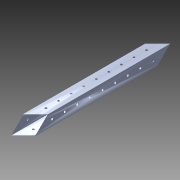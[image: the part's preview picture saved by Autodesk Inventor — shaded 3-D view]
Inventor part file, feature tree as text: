
AUTODESK INVENTOR PART (.ipt)
format: ipt  version: 2014 SP1 (Build 180222100, 222)  size: 1,241,088 bytes
history: native  units: in
note: dims shown in document units (in); Inventor stores cm internally (conversion verified against a paired STEP export)
features: pattern_circular x1, other x1, plane x1, extrude x1, imported_body x1, sketch x1
ambient origin geometry x8: Origin, YZ Plane, XZ Plane, XY Plane, X Axis, Y Axis, Z Axis, Center Point
bodies: Body1 (feature_tree)
feature tree (6):
  pattern_circular  "CirPattern2"
  other  "217-3426-STEP1"
  plane  "Work Plane1"
  extrude  "Extrusion1"  Depth=3937.0079in TaperAngle=0.0deg
  imported_body  "Base1"
  sketch  "Sketch1"  dims[d0=-22.0in d1=3937.0079in d2=0.0in]
